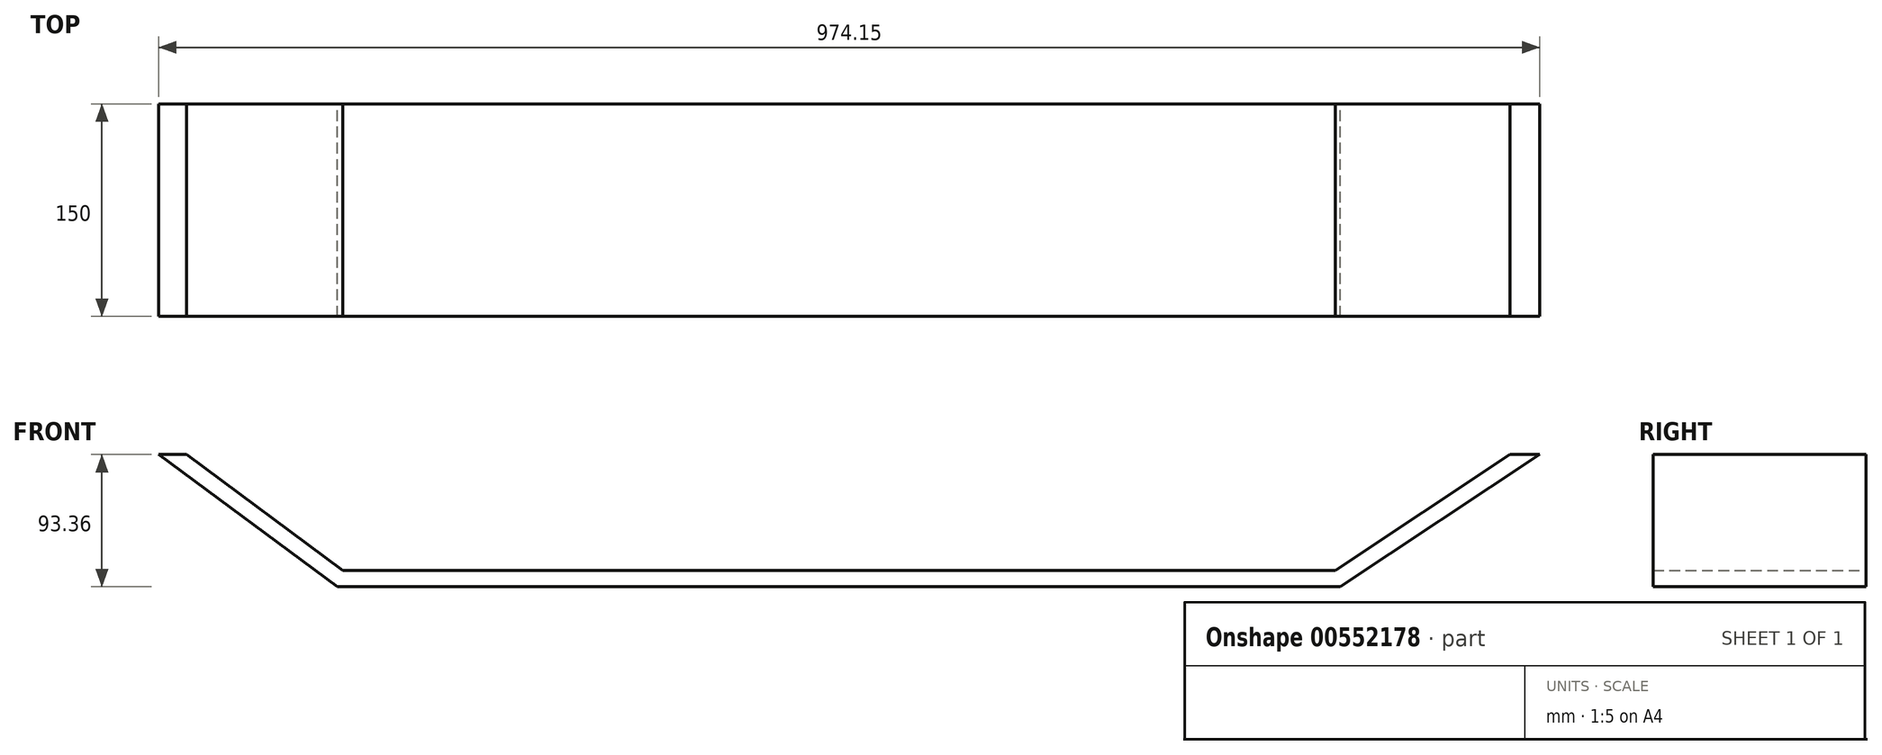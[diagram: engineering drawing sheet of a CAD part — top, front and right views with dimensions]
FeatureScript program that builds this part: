
annotation { "Feature Type Name" : "Feature", "Feature Type Description" : "" }
export const myFeature = defineFeature(function(context is Context, id is Id, definition is map)
    precondition{}
    {
        {
            var Q0;
            Q0=qCreatedBy(makeId("Front.planeOp"),FACE);
            var sketch = newSketch(context, id + "F0", { "sketchPlane" : qUnion([Q0])});
            skLineSegment(sketch, "E0", {"start": v(0, 0) * mm, "end": v(455.48, 0) * mm});
            skLineSegment(sketch, "E1", {"start": v(0, 0) * mm, "end": v(-444.52, 0) * mm});
            skLineSegment(sketch, "E2", {"start": v(0, 0) * mm, "end": v(0, -70) * mm});
            skLineSegment(sketch, "E3", {"start": v(0, -70) * mm, "end": v(350, -70) * mm});
            skLineSegment(sketch, "E4", {"start": v(350, -70) * mm, "end": v(-350, -70) * mm});
            skLineSegment(sketch, "E5", {"start": v(-444.52, 0) * mm, "end": v(-350, -70) * mm});
            skLineSegment(sketch, "E6", {"start": v(350, -70) * mm, "end": v(455.48, 0) * mm});
            skLineSegment(sketch, "E7.0", {"start": v(353.52, -81.68) * mm, "end": v(-353.86, -81.68) * mm});
            skLineSegment(sketch, "E7.1", {"start": v(-479.93, 11.68) * mm, "end": v(-353.86, -81.68) * mm});
            skLineSegment(sketch, "E7.2", {"start": v(353.52, -81.68) * mm, "end": v(494.22, 11.68) * mm});
            skLineSegment(sketch, "E7.3", {"start": v(0, 11.68) * mm, "end": v(494.22, 11.68) * mm});
            skLineSegment(sketch, "E7.4", {"start": v(0, 11.68) * mm, "end": v(-479.93, 11.68) * mm});
            skLineSegment(sketch, "E8", {"start": v(-444.52, 0) * mm, "end": v(-460.3, 11.68) * mm});
            skLineSegment(sketch, "E9", {"start": v(455.48, 0) * mm, "end": v(473.09, 11.68) * mm});
            skSolve(sketch);
        }
        {
            var Q0;
            {var subQ9=sQuery(id+"F0.wireOp",EDGE,"E5");Q0=makeQuery(id+"F0.imprint","IMPRINT",FACE,{"disambiguationData":[TD([[makeQuery(id+"F0.imprint","IMPRINT",EDGE,{"derivedFrom":subQ9}),-1.0]])]});}
            extrude(context, id + "F1", {"entities" : qUnion([Q0]), "depth" : 150 * mm, "offsetDistance" : 25.4 * mm});
        }
    });
